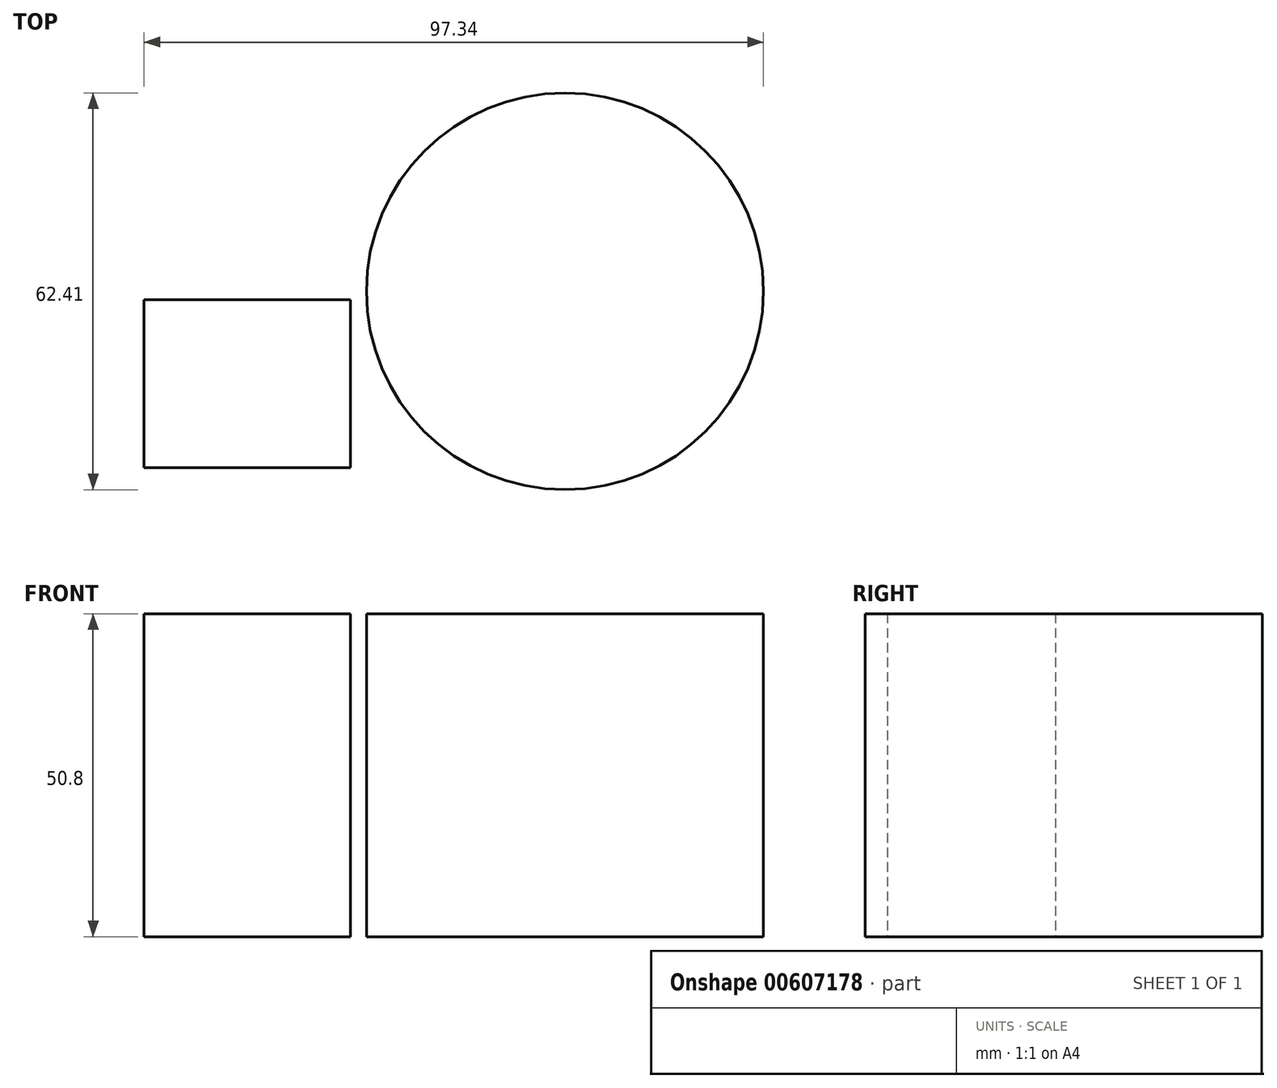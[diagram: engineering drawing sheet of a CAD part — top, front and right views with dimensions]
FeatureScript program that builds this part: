
annotation { "Feature Type Name" : "Feature", "Feature Type Description" : "" }
export const myFeature = defineFeature(function(context is Context, id is Id, definition is map)
    precondition{}
    {
        {
            var Q0;
            Q0=qCreatedBy(makeId("Top.planeOp"),FACE);
            var sketch = newSketch(context, id + "F0", { "sketchPlane" : qUnion([Q0])});
            skLineSegment(sketch, "E0.bottom", {"start": v(-32.4, 29.2) * mm, "end": v(0, 29.2) * mm});
            skLineSegment(sketch, "E0.top", {"start": v(-32.4, 2.8) * mm, "end": v(0, 2.8) * mm});
            skLineSegment(sketch, "E0.left", {"start": v(-32.4, 29.2) * mm, "end": v(-32.4, 2.8) * mm});
            skLineSegment(sketch, "E0.right", {"start": v(0, 29.2) * mm, "end": v(0, 2.8) * mm});
            skCircle(sketch, "E1", {"center": v(33.74, 30.54) * mm, "radius": 31.2 * mm});
            skSolve(sketch);
        }
        {
            var Q0;
            Q0 = qSketchRegion(id + "F0", true);
            extrude(context, id + "F1", {"entities" : qUnion([Q0]), "depth" : 50.8 * mm, "offsetDistance" : 25.4 * mm});
        }
    });
